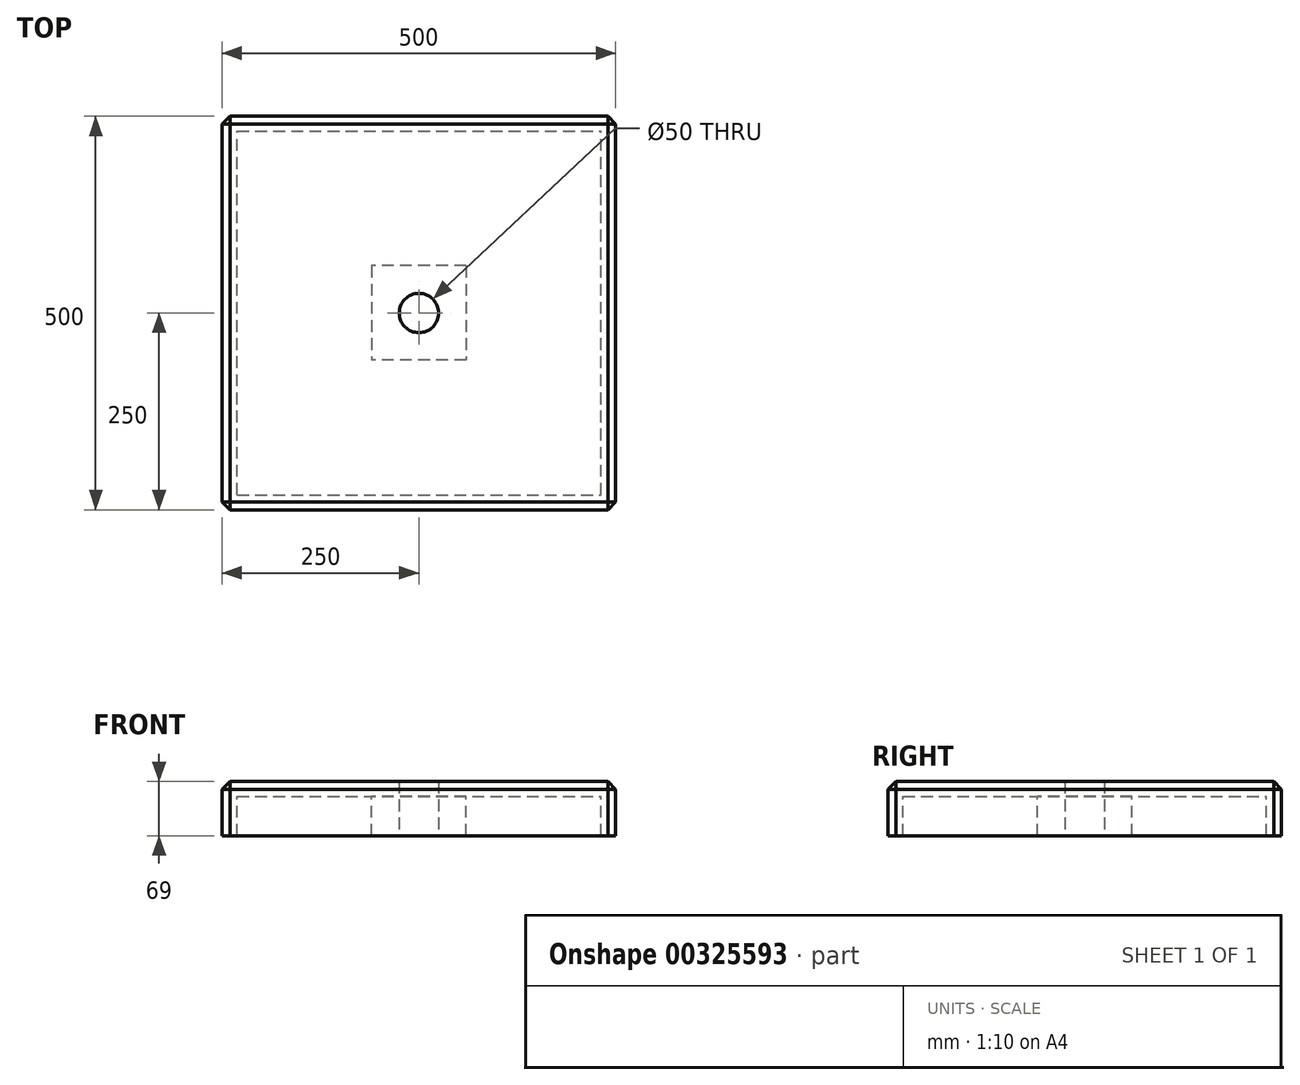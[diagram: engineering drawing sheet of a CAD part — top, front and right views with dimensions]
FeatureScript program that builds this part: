
annotation { "Feature Type Name" : "Feature", "Feature Type Description" : "" }
export const myFeature = defineFeature(function(context is Context, id is Id, definition is map)
    precondition{}
    {
        {
            var Q0;
            Q0=qCreatedBy(makeId("Top.planeOp"),FACE);
            var sketch = newSketch(context, id + "F0", { "sketchPlane" : qUnion([Q0])});
            skLineSegment(sketch, "E0.bottom", {"start": v(250, -250) * mm, "end": v(-250, -250) * mm});
            skLineSegment(sketch, "E0.top", {"start": v(250, 250) * mm, "end": v(-250, 250) * mm});
            skLineSegment(sketch, "E0.left", {"start": v(250, -250) * mm, "end": v(250, 250) * mm});
            skLineSegment(sketch, "E0.right", {"start": v(-250, -250) * mm, "end": v(-250, 250) * mm});
            skPoint(sketch, "E0.middle", {"position": v(0, 0) * mm});
            skCircle(sketch, "E1", {"center": v(0, 0) * mm, "radius": 25 * mm});
            skSolve(sketch);
        }
        {
            var Q0;
            Q0 = qSketchRegion(id + "F0", true);
            extrude(context, id + "F1", {"entities" : qUnion([Q0]), "depth" : 19 * mm});
        }
        {
            var Q0;
            Q0=makeQuery(id+"F1.opExtrude","CAP_FACE",FACE,{"disambiguationData":[OSD([sQuery(id+"F0.wireOp",EDGE,"E0.bottom"),sQuery(id+"F0.wireOp",EDGE,"E0.top"),sQuery(id+"F0.wireOp",EDGE,"E0.left"),sQuery(id+"F0.wireOp",EDGE,"E0.right"),sQuery(id+"F0.wireOp",EDGE,"E1")])],"isStart":true});
            var sketch = newSketch(context, id + "F2", { "sketchPlane" : qUnion([Q0])});
            skLineSegment(sketch, "E2.bottom", {"start": v(-250, 250) * mm, "end": v(250, 250) * mm});
            skLineSegment(sketch, "E2.top", {"start": v(-250, -250) * mm, "end": v(250, -250) * mm});
            skLineSegment(sketch, "E2.left", {"start": v(-250, 250) * mm, "end": v(-250, -250) * mm});
            skLineSegment(sketch, "E2.right", {"start": v(250, 250) * mm, "end": v(250, -250) * mm});
            skLineSegment(sketch, "E3.0", {"start": v(-231, 231) * mm, "end": v(231, 231) * mm});
            skLineSegment(sketch, "E3.1", {"start": v(-231, 231) * mm, "end": v(-231, -231) * mm});
            skLineSegment(sketch, "E3.2", {"start": v(-231, -231) * mm, "end": v(231, -231) * mm});
            skLineSegment(sketch, "E3.3", {"start": v(231, 231) * mm, "end": v(231, -231) * mm});
            skCircle(sketch, "E4", {"center": v(0, 0) * mm, "radius": 25 * mm});
            skPoint(sketch, "E4.first.point", {"position": v(-19.17, 16.05) * mm});
            skPoint(sketch, "E4.second.point", {"position": v(24.07, 6.74) * mm});
            skPoint(sketch, "E4.third.point", {"position": v(9.31, -23.2) * mm});
            skLineSegment(sketch, "E5.bottom", {"start": v(60, -60) * mm, "end": v(-60, -60) * mm});
            skLineSegment(sketch, "E5.top", {"start": v(60, 60) * mm, "end": v(-60, 60) * mm});
            skLineSegment(sketch, "E5.left", {"start": v(60, -60) * mm, "end": v(60, 60) * mm});
            skLineSegment(sketch, "E5.right", {"start": v(-60, -60) * mm, "end": v(-60, 60) * mm});
            skSolve(sketch);
        }
        {
            var Q0;
            Q0 = qSketchRegion(id + "F2", true);
            var Q1;
            Q1=makeQuery(id+"F2.imprint","IMPRINT",FACE,{"disambiguationData":[TD([[makeQuery(id+"F2.imprint","IMPRINT",EDGE,{"derivedFrom":sQuery(id+"F2.wireOp",EDGE,"E4")}),1.0]])]});
            extrude(context, id + "F3", {"entities" : qUnion([Q0, Q1]), "operationType" : NewBodyOperationType.ADD, "depth" : 50 * mm});
        }
        {
            var Q0;
            Q0=makeQuery(id+"F1.opExtrude","CAP_EDGE",EDGE,{"disambiguationData":[OSD([sQuery(id+"F0.wireOp",EDGE,"E0.top")])],"isStart":false});
            var Q1;
            Q1=makeQuery(id+"F1.opExtrude","CAP_EDGE",EDGE,{"disambiguationData":[OSD([sQuery(id+"F0.wireOp",EDGE,"E0.left")])],"isStart":false});
            var Q2;
            Q2=makeQuery(id+"F1.opExtrude","CAP_EDGE",EDGE,{"disambiguationData":[OSD([sQuery(id+"F0.wireOp",EDGE,"E0.bottom")])],"isStart":false});
            var Q3;
            Q3=makeQuery(id+"F1.opExtrude","CAP_EDGE",EDGE,{"disambiguationData":[OSD([sQuery(id+"F0.wireOp",EDGE,"E0.right")])],"isStart":false});
            var Q4;
            Q4=makeQuery(id+"F3.boolean.opBoolean","MERGE",EDGE,{"derivedFrom":[makeQuery(id+"F1.opExtrude","SWEPT_EDGE",EDGE,{"disambiguationData":[OSD([sQuery(id+"F0.wireOp",EDGE,"E0.top"),sQuery(id+"F0.wireOp",EDGE,"E0.right")])]}),makeQuery(id+"F3.opExtrude","SWEPT_EDGE",EDGE,{"disambiguationData":[OSD([sQuery(id+"F2.wireOp",EDGE,"E2.top"),sQuery(id+"F2.wireOp",EDGE,"E2.left")])]})]});
            var Q5;
            Q5=makeQuery(id+"F3.boolean.opBoolean","MERGE",EDGE,{"derivedFrom":[makeQuery(id+"F1.opExtrude","SWEPT_EDGE",EDGE,{"disambiguationData":[OSD([sQuery(id+"F0.wireOp",EDGE,"E0.bottom"),sQuery(id+"F0.wireOp",EDGE,"E0.right")])]}),makeQuery(id+"F3.opExtrude","SWEPT_EDGE",EDGE,{"disambiguationData":[OSD([sQuery(id+"F2.wireOp",EDGE,"E2.bottom"),sQuery(id+"F2.wireOp",EDGE,"E2.left")])]})]});
            var Q6;
            Q6=makeQuery(id+"F3.boolean.opBoolean","MERGE",EDGE,{"derivedFrom":[makeQuery(id+"F1.opExtrude","SWEPT_EDGE",EDGE,{"disambiguationData":[OSD([sQuery(id+"F0.wireOp",EDGE,"E0.top"),sQuery(id+"F0.wireOp",EDGE,"E0.left")])]}),makeQuery(id+"F3.opExtrude","SWEPT_EDGE",EDGE,{"disambiguationData":[OSD([sQuery(id+"F2.wireOp",EDGE,"E2.top"),sQuery(id+"F2.wireOp",EDGE,"E2.right")])]})]});
            var Q7;
            Q7=makeQuery(id+"F3.boolean.opBoolean","MERGE",EDGE,{"derivedFrom":[makeQuery(id+"F1.opExtrude","SWEPT_EDGE",EDGE,{"disambiguationData":[OSD([sQuery(id+"F0.wireOp",EDGE,"E0.bottom"),sQuery(id+"F0.wireOp",EDGE,"E0.left")])]}),makeQuery(id+"F3.opExtrude","SWEPT_EDGE",EDGE,{"disambiguationData":[OSD([sQuery(id+"F2.wireOp",EDGE,"E2.bottom"),sQuery(id+"F2.wireOp",EDGE,"E2.right")])]})]});
            chamfer(context, id + "F4", {"entities" : qUnion([Q0, Q1, Q2, Q3, Q4, Q5, Q6, Q7]), "width" : 10 * mm, "tangentPropagation" : true});
        }
    });
